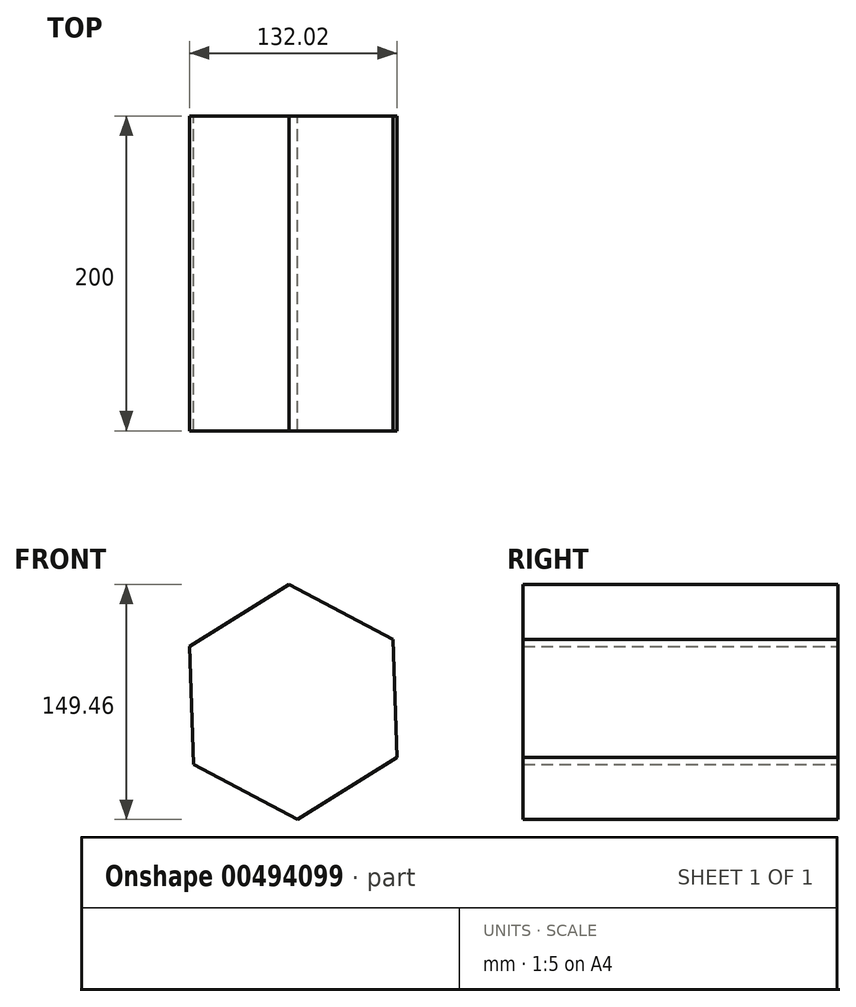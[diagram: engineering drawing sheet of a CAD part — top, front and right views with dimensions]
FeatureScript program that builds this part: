
annotation { "Feature Type Name" : "Feature", "Feature Type Description" : "" }
export const myFeature = defineFeature(function(context is Context, id is Id, definition is map)
    precondition{}
    {
        {
            var Q0;
            Q0=qCreatedBy(makeId("Front.planeOp"),FACE);
            var sketch = newSketch(context, id + "F0", { "sketchPlane" : qUnion([Q0])});
            skCircle(sketch, "E0.cCircle", {"center": v(0, 0) * mm, "radius": 74.78 * mm, "construction": true});
            skLineSegment(sketch, "E0.0", {"start": v(-2.58, 74.73) * mm, "end": v(63.43, 39.6) * mm});
            skLineSegment(sketch, "E0.1", {"start": v(63.43, 39.6) * mm, "end": v(66.01, -35.13) * mm});
            skLineSegment(sketch, "E0.2", {"start": v(66.01, -35.13) * mm, "end": v(2.58, -74.73) * mm});
            skLineSegment(sketch, "E0.3", {"start": v(2.58, -74.73) * mm, "end": v(-63.43, -39.6) * mm});
            skLineSegment(sketch, "E0.4", {"start": v(-63.43, -39.6) * mm, "end": v(-66.01, 35.13) * mm});
            skLineSegment(sketch, "E0.5", {"start": v(-66.01, 35.13) * mm, "end": v(-2.58, 74.73) * mm});
            skSolve(sketch);
        }
        {
            var Q0;
            Q0 = qSketchRegion(id + "F0", true);
            extrude(context, id + "F1", {"entities" : qUnion([Q0]), "depth" : 200 * mm});
        }
    });
